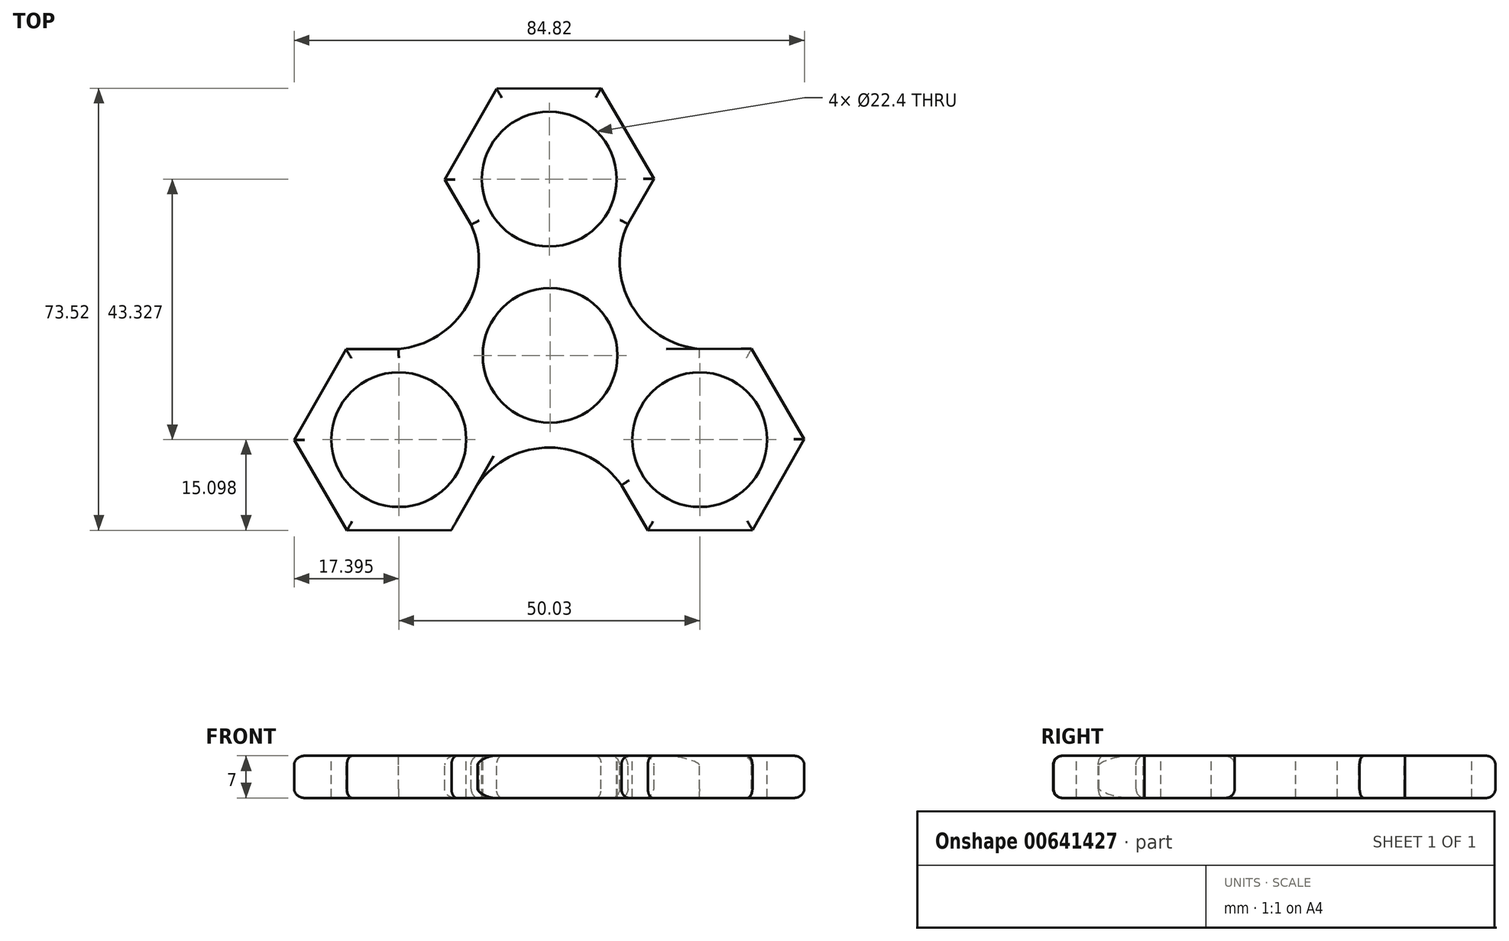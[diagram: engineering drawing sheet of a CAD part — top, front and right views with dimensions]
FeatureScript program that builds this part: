
annotation { "Feature Type Name" : "Feature", "Feature Type Description" : "" }
export const myFeature = defineFeature(function(context is Context, id is Id, definition is map)
    precondition{}
    {
        {
            var Q0;
            Q0=qCreatedBy(makeId("Top.planeOp"),FACE);
            var sketch = newSketch(context, id + "F0", { "sketchPlane" : qUnion([Q0])});
            skCircle(sketch, "E0", {"center": v(0.15, -0.44) * mm, "radius": 11.2 * mm});
            skArc(sketch, "E1", {"start": v(-13.3, -4.98) * mm, "mid": v(10.96, -9.03) * mm, "end": v(2.34, 14) * mm});
            skCircle(sketch, "E2", {"center": v(0, 28.88) * mm, "radius": 11.2 * mm});
            skArc(sketch, "E3.cCircle", {"start": v(-2.34, 14) * mm, "mid": v(0, 13.82) * mm, "end": v(2.34, 14) * mm, "construction": true});
            skLineSegment(sketch, "E3.0", {"start": v(-17.4, 28.8) * mm, "end": v(-8.76, 43.9) * mm});
            skLineSegment(sketch, "E3.1", {"start": v(-8.76, 43.9) * mm, "end": v(8.63, 43.98) * mm});
            skLineSegment(sketch, "E3.2", {"start": v(8.63, 43.98) * mm, "end": v(17.4, 28.96) * mm});
            skLineSegment(sketch, "E3.3", {"start": v(17.4, 28.96) * mm, "end": v(8.76, 13.86) * mm});
            skLineSegment(sketch, "E3.4", {"start": v(8.76, 13.86) * mm, "end": v(-8.63, 13.78) * mm});
            skLineSegment(sketch, "E3.5", {"start": v(-8.63, 13.78) * mm, "end": v(-17.4, 28.8) * mm});
            skPoint(sketch, "E3.0.midPoint", {"position": v(-13.08, 36.36) * mm});
            skLineSegment(sketch, "E4.1.0", {"start": v(-7.62, -14.36) * mm, "end": v(-11.94, -21.91) * mm});
            skLineSegment(sketch, "E4.1.1", {"start": v(-16.25, -29.46) * mm, "end": v(-33.64, -29.54) * mm});
            skLineSegment(sketch, "E4.1.2", {"start": v(-33.64, -29.54) * mm, "end": v(-42.4, -14.52) * mm});
            skArc(sketch, "E4.1.3", {"start": v(-12, -6.85) * mm, "mid": v(-12.62, -5.9) * mm, "end": v(-13.3, -4.98) * mm, "construction": true});
            skLineSegment(sketch, "E4.1.4", {"start": v(-42.4, -14.52) * mm, "end": v(-33.78, 0.58) * mm});
            skLineSegment(sketch, "E4.2.0", {"start": v(16.25, 0.58) * mm, "end": v(33.64, 0.66) * mm});
            skLineSegment(sketch, "E4.2.1", {"start": v(33.64, 0.66) * mm, "end": v(42.4, -14.36) * mm});
            skLineSegment(sketch, "E4.2.2", {"start": v(42.4, -14.36) * mm, "end": v(33.78, -29.46) * mm});
            skLineSegment(sketch, "E4.2.4", {"start": v(33.78, -29.46) * mm, "end": v(16.39, -29.54) * mm});
            skCircle(sketch, "E5.1.0", {"center": v(-25.01, -14.44) * mm, "radius": 11.2 * mm});
            skCircle(sketch, "E5.2.0", {"center": v(25.01, -14.44) * mm, "radius": 11.2 * mm});
            skArc(sketch, "E6.trimOffspring", {"start": v(13.3, -4.98) * mm, "mid": v(11.97, -6.91) * mm, "end": v(10.96, -9.03) * mm, "construction": true});
            skLineSegment(sketch, "E7", {"start": v(-16.25, -29.46) * mm, "end": v(-11.94, -21.91) * mm});
            skLineSegment(sketch, "E8.1.0", {"start": v(-16.39, 0.66) * mm, "end": v(-7.62, -14.36) * mm});
            skLineSegment(sketch, "E8.1.2", {"start": v(-33.78, 0.58) * mm, "end": v(-16.39, 0.66) * mm});
            skLineSegment(sketch, "E8.1.4", {"start": v(-7.62, -14.36) * mm, "end": v(-16.25, -29.46) * mm});
            skLineSegment(sketch, "E8.2.0", {"start": v(7.62, -14.52) * mm, "end": v(10.39, -9.68) * mm});
            skLineSegment(sketch, "E8.2.2", {"start": v(16.39, -29.54) * mm, "end": v(7.62, -14.52) * mm});
            skArc(sketch, "E9", {"start": v(-25.08, 0.62) * mm, "mid": v(-13.7, 7.83) * mm, "end": v(-13.01, 21.3) * mm});
            skArc(sketch, "E10.1.0", {"start": v(12, -22.03) * mm, "mid": v(0.06, -15.77) * mm, "end": v(-11.94, -21.91) * mm});
            skArc(sketch, "E10.2.0", {"start": v(13.08, 21.41) * mm, "mid": v(13.63, 7.94) * mm, "end": v(24.95, 0.62) * mm});
            skLineSegment(sketch, "E11.trimOffspring", {"start": v(13.61, -4.03) * mm, "end": v(16.25, 0.58) * mm});
            skArc(sketch, "E12.trimOffspring", {"start": v(-2.34, 14) * mm, "mid": v(-12.08, 7.47) * mm, "end": v(-13.58, -4.16) * mm});
            skSolve(sketch);
        }
        {
            var Q0;
            Q0=makeQuery(id+"F0.imprint","IMPRINT",FACE,{"disambiguationData":[TD([[makeQuery(id+"F0.imprint","IMPRINT",EDGE,{"derivedFrom":sQuery(id+"F0.wireOp",EDGE,"E0")}),-1.0]])]});
            var Q1;
            Q1=makeQuery(id+"F0.imprint","IMPRINT",FACE,{"disambiguationData":[TD([[makeQuery(id+"F0.imprint","IMPRINT",EDGE,{"derivedFrom":sQuery(id+"F0.wireOp",EDGE,"E4.2.2")}),-1.0]])]});
            var Q2;
            {var subQ9=sQuery(id+"F0.wireOp",EDGE,"E10.2.0");Q2=makeQuery(id+"F0.imprint","IMPRINT",FACE,{"disambiguationData":[TD([[makeQuery(id+"F0.imprint","IMPRINT",EDGE,{"derivedFrom":subQ9}),-1.0]])]});}
            var Q3;
            Q3=makeQuery(id+"F0.imprint","IMPRINT",FACE,{"disambiguationData":[TD([[makeQuery(id+"F0.imprint","IMPRINT",EDGE,{"derivedFrom":sQuery(id+"F0.wireOp",EDGE,"E2")}),-1.0]])]});
            var Q4;
            Q4=makeQuery(id+"F0.imprint","IMPRINT",FACE,{"disambiguationData":[TD([[makeQuery(id+"F0.imprint","IMPRINT",EDGE,{"derivedFrom":sQuery(id+"F0.wireOp",EDGE,"E4.1.2")}),-1.0]])]});
            var Q5;
            {var subQ5=sQuery(id+"F0.wireOp",EDGE,"E10.1.0");Q5=makeQuery(id+"F0.imprint","IMPRINT",FACE,{"disambiguationData":[TD([[makeQuery(id+"F0.imprint","IMPRINT",EDGE,{"derivedFrom":subQ5}),-1.0]])]});}
            var Q6;
            {var subQ3=sQuery(id+"F0.wireOp",EDGE,"E9");Q6=makeQuery(id+"F0.imprint","IMPRINT",FACE,{"disambiguationData":[TD([[makeQuery(id+"F0.imprint","IMPRINT",EDGE,{"derivedFrom":subQ3}),-1.0]])]});}
            extrude(context, id + "F1", {"entities" : qUnion([Q0, Q1, Q2, Q3, Q4, Q5, Q6]), "oppositeDirection" : true, "depth" : 7 * mm, "offsetDistance" : 25 * mm});
        }
        {
            var Q0;
            Q0=makeQuery(id+"F1.opExtrude","CAP_EDGE",EDGE,{"disambiguationData":[OSD([sQuery(id+"F0.wireOp",EDGE,"E9")])],"isStart":true});
            var Q1;
            Q1=makeQuery(id+"F1.opExtrude","CAP_EDGE",EDGE,{"disambiguationData":[OSD([sQuery(id+"F0.wireOp",EDGE,"E8.1.2")])],"isStart":true});
            var Q2;
            Q2=makeQuery(id+"F1.opExtrude","CAP_EDGE",EDGE,{"disambiguationData":[OSD([sQuery(id+"F0.wireOp",EDGE,"E4.1.4")])],"isStart":true});
            var Q3;
            Q3=makeQuery(id+"F1.opExtrude","CAP_EDGE",EDGE,{"disambiguationData":[OSD([sQuery(id+"F0.wireOp",EDGE,"E4.1.2")])],"isStart":true});
            var Q4;
            Q4=makeQuery(id+"F1.opExtrude","CAP_EDGE",EDGE,{"disambiguationData":[OSD([sQuery(id+"F0.wireOp",EDGE,"E4.1.1")])],"isStart":true});
            var Q5;
            Q5=makeQuery(id+"F1.opExtrude","CAP_EDGE",EDGE,{"disambiguationData":[OSD([sQuery(id+"F0.wireOp",EDGE,"E10.1.0")])],"isStart":true});
            var Q6;
            Q6=makeQuery(id+"F1.opExtrude","CAP_EDGE",EDGE,{"disambiguationData":[OSD([sQuery(id+"F0.wireOp",EDGE,"E8.1.4")])],"isStart":true});
            var Q7;
            Q7=makeQuery(id+"F1.opExtrude","CAP_EDGE",EDGE,{"disambiguationData":[OSD([sQuery(id+"F0.wireOp",EDGE,"E8.2.2")])],"isStart":true});
            var Q8;
            Q8=makeQuery(id+"F1.opExtrude","CAP_EDGE",EDGE,{"disambiguationData":[OSD([sQuery(id+"F0.wireOp",EDGE,"E4.2.4")])],"isStart":true});
            var Q9;
            Q9=makeQuery(id+"F1.opExtrude","CAP_EDGE",EDGE,{"disambiguationData":[OSD([sQuery(id+"F0.wireOp",EDGE,"E4.2.2")])],"isStart":true});
            var Q10;
            Q10=makeQuery(id+"F1.opExtrude","CAP_EDGE",EDGE,{"disambiguationData":[OSD([sQuery(id+"F0.wireOp",EDGE,"E4.2.1")])],"isStart":true});
            var Q11;
            Q11=makeQuery(id+"F1.opExtrude","CAP_EDGE",EDGE,{"disambiguationData":[OSD([sQuery(id+"F0.wireOp",EDGE,"E10.2.0")])],"isStart":true});
            var Q12;
            Q12=makeQuery(id+"F1.opExtrude","CAP_EDGE",EDGE,{"disambiguationData":[OSD([sQuery(id+"F0.wireOp",EDGE,"E3.3")])],"isStart":true});
            var Q13;
            Q13=makeQuery(id+"F1.opExtrude","CAP_EDGE",EDGE,{"disambiguationData":[OSD([sQuery(id+"F0.wireOp",EDGE,"E3.2")])],"isStart":true});
            var Q14;
            Q14=makeQuery(id+"F1.opExtrude","CAP_EDGE",EDGE,{"disambiguationData":[OSD([sQuery(id+"F0.wireOp",EDGE,"E3.0")])],"isStart":true});
            var Q15;
            Q15=makeQuery(id+"F1.opExtrude","CAP_EDGE",EDGE,{"disambiguationData":[OSD([sQuery(id+"F0.wireOp",EDGE,"E3.1")])],"isStart":true});
            var Q16;
            Q16=makeQuery(id+"F1.opExtrude","CAP_EDGE",EDGE,{"disambiguationData":[OSD([sQuery(id+"F0.wireOp",EDGE,"E3.5")])],"isStart":true});
            fillet(context, id + "F2", {"entities" : qUnion([Q0, Q1, Q2, Q3, Q4, Q5, Q6, Q7, Q8, Q9, Q10, Q11, Q12, Q13, Q14, Q15, Q16]), "radius" : 1.5 * mm, "tangentPropagation" : true, "allowEdgeOverflow" : false});
        }
        {
            var Q0;
            Q0=makeQuery(id+"F1.opExtrude","CAP_EDGE",EDGE,{"disambiguationData":[OSD([sQuery(id+"F0.wireOp",EDGE,"E10.1.0")])],"isStart":false});
            var Q1;
            Q1=makeQuery(id+"F1.opExtrude","CAP_EDGE",EDGE,{"disambiguationData":[OSD([sQuery(id+"F0.wireOp",EDGE,"E8.1.4")])],"isStart":false});
            var Q2;
            Q2=makeQuery(id+"F1.opExtrude","CAP_EDGE",EDGE,{"disambiguationData":[OSD([sQuery(id+"F0.wireOp",EDGE,"E4.1.1")])],"isStart":false});
            var Q3;
            Q3=makeQuery(id+"F1.opExtrude","CAP_EDGE",EDGE,{"disambiguationData":[OSD([sQuery(id+"F0.wireOp",EDGE,"E4.1.2")])],"isStart":false});
            var Q4;
            Q4=makeQuery(id+"F1.opExtrude","CAP_EDGE",EDGE,{"disambiguationData":[OSD([sQuery(id+"F0.wireOp",EDGE,"E4.1.4")])],"isStart":false});
            var Q5;
            Q5=makeQuery(id+"F1.opExtrude","CAP_EDGE",EDGE,{"disambiguationData":[OSD([sQuery(id+"F0.wireOp",EDGE,"E8.1.2")])],"isStart":false});
            var Q6;
            Q6=makeQuery(id+"F1.opExtrude","CAP_EDGE",EDGE,{"disambiguationData":[OSD([sQuery(id+"F0.wireOp",EDGE,"E9")])],"isStart":false});
            var Q7;
            Q7=makeQuery(id+"F1.opExtrude","CAP_EDGE",EDGE,{"disambiguationData":[OSD([sQuery(id+"F0.wireOp",EDGE,"E3.5")])],"isStart":false});
            var Q8;
            Q8=makeQuery(id+"F1.opExtrude","CAP_EDGE",EDGE,{"disambiguationData":[OSD([sQuery(id+"F0.wireOp",EDGE,"E3.0")])],"isStart":false});
            var Q9;
            Q9=makeQuery(id+"F1.opExtrude","CAP_EDGE",EDGE,{"disambiguationData":[OSD([sQuery(id+"F0.wireOp",EDGE,"E3.1")])],"isStart":false});
            var Q10;
            Q10=makeQuery(id+"F1.opExtrude","CAP_EDGE",EDGE,{"disambiguationData":[OSD([sQuery(id+"F0.wireOp",EDGE,"E3.2")])],"isStart":false});
            var Q11;
            Q11=makeQuery(id+"F1.opExtrude","CAP_EDGE",EDGE,{"disambiguationData":[OSD([sQuery(id+"F0.wireOp",EDGE,"E3.3")])],"isStart":false});
            var Q12;
            Q12=makeQuery(id+"F1.opExtrude","CAP_EDGE",EDGE,{"disambiguationData":[OSD([sQuery(id+"F0.wireOp",EDGE,"E10.2.0")])],"isStart":false});
            var Q13;
            Q13=makeQuery(id+"F1.opExtrude","CAP_EDGE",EDGE,{"disambiguationData":[OSD([sQuery(id+"F0.wireOp",EDGE,"E4.2.0")])],"isStart":false});
            var Q14;
            Q14=makeQuery(id+"F1.opExtrude","CAP_EDGE",EDGE,{"disambiguationData":[OSD([sQuery(id+"F0.wireOp",EDGE,"E4.2.1")])],"isStart":false});
            var Q15;
            Q15=makeQuery(id+"F1.opExtrude","CAP_EDGE",EDGE,{"disambiguationData":[OSD([sQuery(id+"F0.wireOp",EDGE,"E4.2.2")])],"isStart":false});
            var Q16;
            Q16=makeQuery(id+"F1.opExtrude","CAP_EDGE",EDGE,{"disambiguationData":[OSD([sQuery(id+"F0.wireOp",EDGE,"E8.2.2")])],"isStart":false});
            var Q17;
            Q17=makeQuery(id+"F1.opExtrude","CAP_EDGE",EDGE,{"disambiguationData":[OSD([sQuery(id+"F0.wireOp",EDGE,"E4.2.4")])],"isStart":false});
            fillet(context, id + "F3", {"entities" : qUnion([Q0, Q1, Q2, Q3, Q4, Q5, Q6, Q7, Q8, Q9, Q10, Q11, Q12, Q13, Q14, Q15, Q16, Q17]), "radius" : 1.5 * mm, "tangentPropagation" : true, "allowEdgeOverflow" : false});
        }
    });
